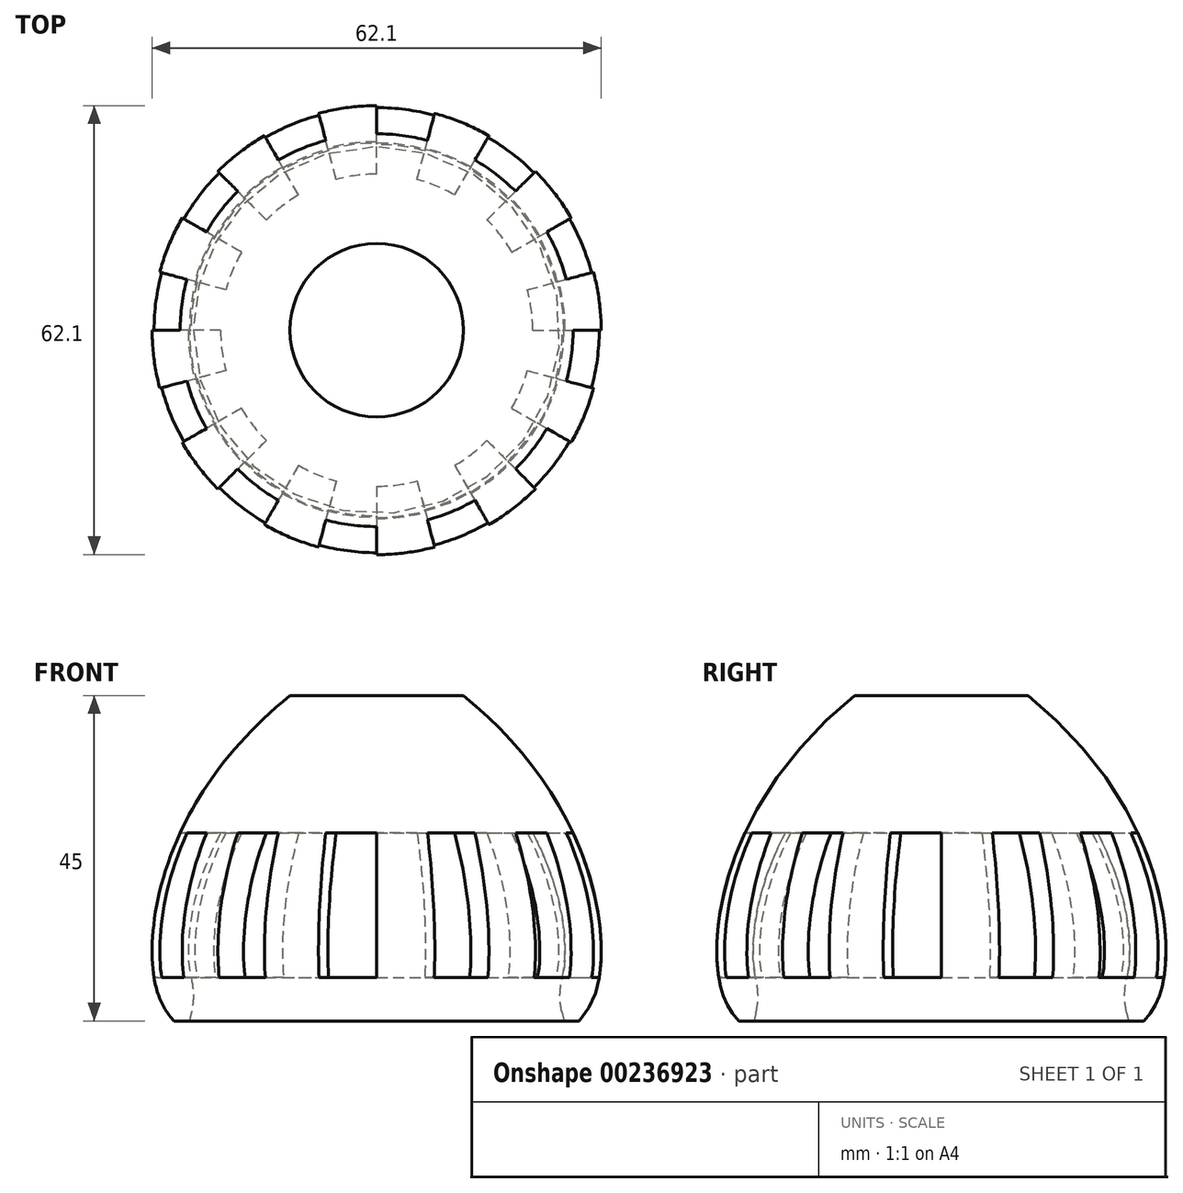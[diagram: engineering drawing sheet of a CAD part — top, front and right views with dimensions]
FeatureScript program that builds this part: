
annotation { "Feature Type Name" : "Feature", "Feature Type Description" : "" }
export const myFeature = defineFeature(function(context is Context, id is Id, definition is map)
    precondition{}
    {
        {
            var Q0;
            Q0=qCreatedBy(makeId("Front.planeOp"),FACE);
            var sketch = newSketch(context, id + "F0", { "sketchPlane" : qUnion([Q0])});
            skLineSegment(sketch, "E0", {"start": v(0, 0) * mm, "end": v(0, 45) * mm});
            skLineSegment(sketch, "E1", {"start": v(0, 45) * mm, "end": v(12, 45) * mm});
            skLineSegment(sketch, "E2", {"start": v(0, 0) * mm, "end": v(28, 0) * mm});
            skLineSegment(sketch, "E3", {"start": v(28, 0) * mm, "end": v(28, 8) * mm, "construction": true});
            skLineSegment(sketch, "E4", {"start": v(28, 8) * mm, "end": v(31, 8) * mm, "construction": true});
            skFitSpline(sketch, "E5", {"points": [v(12, 45) * mm, v(31, 8) * mm, v(28, 0) * mm], "startDerivative": vector(69.76, -56.68) * mm, "endDerivative": vector(-16.2, -16.73) * mm});
            skSolve(sketch);
        }
        {
            var Q0;
            Q0=qSketchRegion(id+"F0",true);
            var Q1;
            Q1=sQuery(id+"F0.wireOp",EDGE,"E0");
            revolve(context, id + "F1", {"entities" : qUnion([Q0]), "axis" : qUnion([Q1]), "revolveType" : RevolveType.FULL});
        }
        {
            var Q0;
            Q0=makeQuery(id+"F1.opRevolve","SWEPT_FACE",FACE,{"disambiguationData":[OSD([sQuery(id+"F0.wireOp",EDGE,"E2")])]});
            shell(context, id + "F2", {"entities" : qUnion([Q0]), "thickness" : 5 * mm});
        }
        {
            var Q0;
            Q0=qCreatedBy(makeId("Top.planeOp"),FACE);
            cPlane(context, id + "F3", {"entities" : qUnion([Q0]), "cplaneType" : CPlaneType.OFFSET, "offset" : 26 * mm, "width" : 150 * mm, "height" : 150 * mm});
        }
        {
            var Q0;
            Q0=qCreatedBy(id+"F3.planeOp",FACE);
            var sketch = newSketch(context, id + "F4", { "sketchPlane" : qUnion([Q0])});
            skCircle(sketch, "E6", {"center": v(0, 0) * mm, "radius": 27.24 * mm});
            skSolve(sketch);
        }
        {
            var Q0;
            Q0=qSketchRegion(id+"F4",true);
            var Q1;
            Q1=makeQuery(id+"F1.opRevolve","SWEPT_BODY",BODY,{"disambiguationData":[OSD([sQuery(id+"F0.wireOp",EDGE,"E0"),sQuery(id+"F0.wireOp",EDGE,"E1"),sQuery(id+"F0.wireOp",EDGE,"E2"),sQuery(id+"F0.wireOp",EDGE,"E5")])]});
            extrude(context, id + "F5", {"entities" : qUnion([Q0]), "operationType" : NewBodyOperationType.ADD, "endBound" : BoundingType.UP_TO_BODY, "endBoundEntityBody" : qUnion([Q1]), "depth" : 25 * mm});
        }
        {
            var Q0;
            Q0=makeQuery(id+"F2.opShell","OFFSET_EDGE",EDGE,{"disambiguationData":[OSD([sQuery(id+"F0.wireOp",EDGE,"E2"),sQuery(id+"F0.wireOp",EDGE,"E5")])]});
            chamfer(context, id + "F6", {"entities" : qUnion([Q0]), "chamferType" : ChamferType.TWO_OFFSETS, "width1" : 6 * mm, "oppositeDirection" : false, "width2" : 5 * mm, "tangentPropagation" : true});
        }
        {
            var Q0;
            {var subQ0=sQuery(id+"F0.wireOp",EDGE,"E5");Q0=makeQuery(id+"F6.opChamfer","BLEND_EDGE",EDGE,{"blendedFrom":[makeQuery(id+"F2.opShell","OFFSET_EDGE",EDGE,{"disambiguationData":[OSD([sQuery(id+"F0.wireOp",EDGE,"E2"),subQ0])]}),makeQuery(id+"F2.opShell","OFFSET_FACE",FACE,{"disambiguationData":[OSD([subQ0])]})],"blendedInto":[makeQuery(id+"F2.opShell","OFFSET_FACE",FACE,{"disambiguationData":[OSD([subQ0])]})]});}
            fillet(context, id + "F7", {"entities" : qUnion([Q0]), "radius" : 10 * mm, "tangentPropagation" : true, "allowEdgeOverflow" : false});
        }
        {
            var Q0;
            Q0=qCreatedBy(makeId("Top.planeOp"),FACE);
            cPlane(context, id + "F8", {"entities" : qUnion([Q0]), "cplaneType" : CPlaneType.OFFSET, "offset" : 6 * mm, "width" : 150 * mm, "height" : 150 * mm});
        }
        {
            var Q0;
            Q0=qCreatedBy(id+"F8.planeOp",FACE);
            var sketch = newSketch(context, id + "F9", { "sketchPlane" : qUnion([Q0])});
            skCircle(sketch, "E7", {"center": v(0, 0) * mm, "radius": 37.97 * mm});
            skLineSegment(sketch, "E8", {"start": v(0, 0) * mm, "end": v(0, -37.97) * mm});
            skLineSegment(sketch, "E9.1.0", {"start": v(0, 0) * mm, "end": v(9.83, -36.68) * mm});
            skLineSegment(sketch, "E9.2.0", {"start": v(0, 0) * mm, "end": v(18.99, -32.89) * mm});
            skLineSegment(sketch, "E9.3.0", {"start": v(0, 0) * mm, "end": v(26.85, -26.85) * mm});
            skLineSegment(sketch, "E9.4.0", {"start": v(0, 0) * mm, "end": v(32.89, -18.99) * mm});
            skLineSegment(sketch, "E9.5.0", {"start": v(0, 0) * mm, "end": v(36.68, -9.83) * mm});
            skLineSegment(sketch, "E9.6.0", {"start": v(0, 0) * mm, "end": v(37.97, 0) * mm});
            skLineSegment(sketch, "E9.7.0", {"start": v(0, 0) * mm, "end": v(36.68, 9.83) * mm});
            skLineSegment(sketch, "E9.8.0", {"start": v(0, 0) * mm, "end": v(32.89, 18.99) * mm});
            skLineSegment(sketch, "E9.9.0", {"start": v(0, 0) * mm, "end": v(26.85, 26.85) * mm});
            skLineSegment(sketch, "E9.10.0", {"start": v(0, 0) * mm, "end": v(18.99, 32.89) * mm});
            skLineSegment(sketch, "E9.11.0", {"start": v(0, 0) * mm, "end": v(9.83, 36.68) * mm});
            skLineSegment(sketch, "E9.12.0", {"start": v(0, 0) * mm, "end": v(0, 37.97) * mm});
            skLineSegment(sketch, "E9.13.0", {"start": v(0, 0) * mm, "end": v(-9.83, 36.68) * mm});
            skLineSegment(sketch, "E9.14.0", {"start": v(0, 0) * mm, "end": v(-18.99, 32.89) * mm});
            skLineSegment(sketch, "E9.15.0", {"start": v(0, 0) * mm, "end": v(-26.85, 26.85) * mm});
            skLineSegment(sketch, "E9.16.0", {"start": v(0, 0) * mm, "end": v(-32.89, 18.99) * mm});
            skLineSegment(sketch, "E9.17.0", {"start": v(0, 0) * mm, "end": v(-36.68, 9.83) * mm});
            skLineSegment(sketch, "E9.18.0", {"start": v(0, 0) * mm, "end": v(-37.97, 0) * mm});
            skLineSegment(sketch, "E9.19.0", {"start": v(0, 0) * mm, "end": v(-36.68, -9.83) * mm});
            skLineSegment(sketch, "E9.20.0", {"start": v(0, 0) * mm, "end": v(-32.89, -18.99) * mm});
            skLineSegment(sketch, "E9.21.0", {"start": v(0, 0) * mm, "end": v(-26.85, -26.85) * mm});
            skLineSegment(sketch, "E9.22.0", {"start": v(0, 0) * mm, "end": v(-18.99, -32.89) * mm});
            skLineSegment(sketch, "E9.23.0", {"start": v(0, 0) * mm, "end": v(-9.83, -36.68) * mm});
            skSolve(sketch);
        }
        {
            var Q0;
            {var subQ0=sQuery(id+"F9.wireOp",EDGE,"E8");Q0=makeQuery(id+"F9.imprint","IMPRINT",FACE,{"disambiguationData":[TD([[makeQuery(id+"F9.imprint","IMPRINT",EDGE,{"derivedFrom":subQ0}),-1.0]])]});}
            var Q1;
            {var subQ0=sQuery(id+"F9.wireOp",EDGE,"E9.21.0");Q1=makeQuery(id+"F9.imprint","IMPRINT",FACE,{"disambiguationData":[TD([[makeQuery(id+"F9.imprint","IMPRINT",EDGE,{"derivedFrom":subQ0}),1.0]])]});}
            var Q2;
            {var subQ0=sQuery(id+"F9.wireOp",EDGE,"E9.19.0");Q2=makeQuery(id+"F9.imprint","IMPRINT",FACE,{"disambiguationData":[TD([[makeQuery(id+"F9.imprint","IMPRINT",EDGE,{"derivedFrom":subQ0}),1.0]])]});}
            var Q3;
            {var subQ0=sQuery(id+"F9.wireOp",EDGE,"E9.17.0");Q3=makeQuery(id+"F9.imprint","IMPRINT",FACE,{"disambiguationData":[TD([[makeQuery(id+"F9.imprint","IMPRINT",EDGE,{"derivedFrom":subQ0}),1.0]])]});}
            var Q4;
            {var subQ0=sQuery(id+"F9.wireOp",EDGE,"E9.15.0");Q4=makeQuery(id+"F9.imprint","IMPRINT",FACE,{"disambiguationData":[TD([[makeQuery(id+"F9.imprint","IMPRINT",EDGE,{"derivedFrom":subQ0}),1.0]])]});}
            var Q5;
            {var subQ0=sQuery(id+"F9.wireOp",EDGE,"E9.13.0");Q5=makeQuery(id+"F9.imprint","IMPRINT",FACE,{"disambiguationData":[TD([[makeQuery(id+"F9.imprint","IMPRINT",EDGE,{"derivedFrom":subQ0}),1.0]])]});}
            var Q6;
            {var subQ0=sQuery(id+"F9.wireOp",EDGE,"E9.11.0");Q6=makeQuery(id+"F9.imprint","IMPRINT",FACE,{"disambiguationData":[TD([[makeQuery(id+"F9.imprint","IMPRINT",EDGE,{"derivedFrom":subQ0}),1.0]])]});}
            var Q7;
            {var subQ0=sQuery(id+"F9.wireOp",EDGE,"E9.9.0");Q7=makeQuery(id+"F9.imprint","IMPRINT",FACE,{"disambiguationData":[TD([[makeQuery(id+"F9.imprint","IMPRINT",EDGE,{"derivedFrom":subQ0}),1.0]])]});}
            var Q8;
            {var subQ0=sQuery(id+"F9.wireOp",EDGE,"E9.7.0");Q8=makeQuery(id+"F9.imprint","IMPRINT",FACE,{"disambiguationData":[TD([[makeQuery(id+"F9.imprint","IMPRINT",EDGE,{"derivedFrom":subQ0}),1.0]])]});}
            var Q9;
            {var subQ0=sQuery(id+"F9.wireOp",EDGE,"E9.5.0");Q9=makeQuery(id+"F9.imprint","IMPRINT",FACE,{"disambiguationData":[TD([[makeQuery(id+"F9.imprint","IMPRINT",EDGE,{"derivedFrom":subQ0}),1.0]])]});}
            var Q10;
            {var subQ0=sQuery(id+"F9.wireOp",EDGE,"E9.3.0");Q10=makeQuery(id+"F9.imprint","IMPRINT",FACE,{"disambiguationData":[TD([[makeQuery(id+"F9.imprint","IMPRINT",EDGE,{"derivedFrom":subQ0}),1.0]])]});}
            var Q11;
            {var subQ0=sQuery(id+"F9.wireOp",EDGE,"E9.1.0");Q11=makeQuery(id+"F9.imprint","IMPRINT",FACE,{"disambiguationData":[TD([[makeQuery(id+"F9.imprint","IMPRINT",EDGE,{"derivedFrom":subQ0}),1.0]])]});}
            var Q12;
            Q12=makeQuery(id+"F5.opExtrude","CAP_FACE",FACE,{"disambiguationData":[OSD([sQuery(id+"F4.wireOp",EDGE,"E6")])],"isStart":true});
            extrude(context, id + "F10", {"entities" : qUnion([Q0, Q1, Q2, Q3, Q4, Q5, Q6, Q7, Q8, Q9, Q10, Q11]), "operationType" : NewBodyOperationType.REMOVE, "endBound" : BoundingType.UP_TO_SURFACE, "endBoundEntityFace" : qUnion([Q12]), "depth" : 25 * mm});
        }
    });
